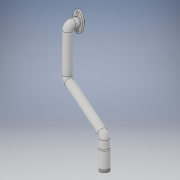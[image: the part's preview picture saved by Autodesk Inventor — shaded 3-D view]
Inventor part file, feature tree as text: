
AUTODESK INVENTOR PART (.ipt)
format: ipt  version: 2018 (Build 220112000, 112)  size: 200,192 bytes
history: native  units: mm
features: sketch x6, extrude x2, plane x2, fillet x2, sweep x1, thread x1
ambient origin geometry x8: Origin, YZ Plane, XZ Plane, XY Plane, X Axis, Y Axis, Z Axis, Center Point
bodies: Solid1 (feature_tree)
feature tree (14):
  extrude  "Extrusion1"  Depth=6.0mm
  sketch  "Sketch2"  dims[d2=7.0mm d3=3.0mm]
  plane  "Work Plane1"
  extrude  "Extrusion2"  Depth=7.0mm
  sketch  "Sketch4"  dims[d11=60.0mm]
  plane  "Work Plane2"
  sketch  "Sketch5"  dims[d12=25.0mm d13=9.0mm d14=7.0mm d15=18.0mm d16=0.0mm d17=8.0mm d18=45.0mm d19=12.0mm d20=12.0mm d21=5.0mm d22=5.0mm d23=5.0mm d24=0.0mm d25=0.0mm d26=0.5mm d27=1.0mm d28=3.0mm d29=15.0mm]
  sweep  "Sweep1"
  fillet  "Fillet1"  Radius=2.0mm
  fillet  "Fillet2"  Radius=10.0mm
  thread  "Thread1"  [1 undecoded]
  sketch  "Sketch1"  dims[d0=10.0mm d1=6.0mm]
  sketch  "Sketch3"  dims[d4=7.0mm d5=2.0mm d6=0.0mm d7=2.0mm d9=10.0mm d10=-100.0mm]
  sketch  "3D Sketch1"
note: 1 required parameter value undecoded (feature->parameter linkage not recoverable at this tier; creation-order binding heuristic only, values carry confidence <= 0.55)
